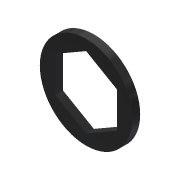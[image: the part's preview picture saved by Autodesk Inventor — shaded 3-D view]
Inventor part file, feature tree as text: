
AUTODESK INVENTOR PART (.ipt)
format: ipt  version: 2013 (Build 170138000, 138)  size: 80,384 bytes
history: native  units: in
note: dims shown in document units (in); Inventor stores cm internally (conversion verified against a paired STEP export)
features: extrude x1, sketch x1
ambient origin geometry x8: Origin, YZ Plane, XZ Plane, XY Plane, X Axis, Y Axis, Z Axis, Center Point
bodies: Solid1 (feature_tree)
feature tree (2):
  extrude  "Extrusion1"  Depth=0.5in
  sketch  "Sketch1"  dims[d0=0.75in d2=0.5in d3=0.063in d4=0.0in]
